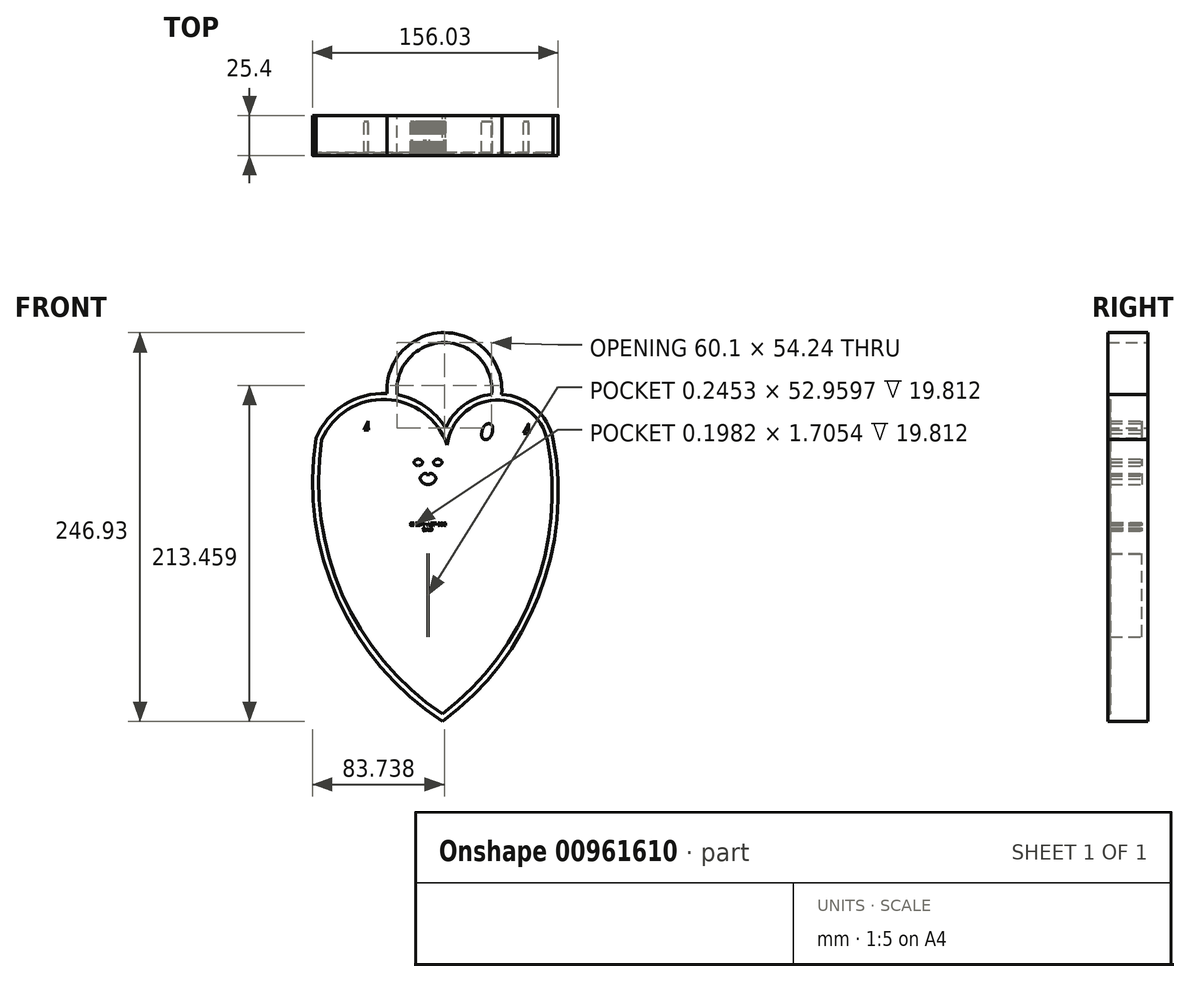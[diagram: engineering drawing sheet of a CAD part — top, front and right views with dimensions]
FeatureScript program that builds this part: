
annotation { "Feature Type Name" : "Feature", "Feature Type Description" : "" }
export const myFeature = defineFeature(function(context is Context, id is Id, definition is map)
    precondition{}
    {
        {
            var Q0;
            Q0=qCreatedBy(makeId("Front.planeOp"),FACE);
            var sketch = newSketch(context, id + "F0", { "sketchPlane" : qUnion([Q0])});
            skArc(sketch, "E0", {"start": v(8.37, 92.35) * mm, "mid": v(-4.85, 106.15) * mm, "end": v(-22.5, 113.49) * mm});
            skArc(sketch, "E1", {"start": v(76.68, 85.17) * mm, "mid": v(65.13, 104.96) * mm, "end": v(43.99, 113.8) * mm});
            skArc(sketch, "E2", {"start": v(6.5, -93.99) * mm, "mid": v(67.39, -14.51) * mm, "end": v(76.68, 85.17) * mm});
            skArc(sketch, "E3", {"start": v(-74.04, 85.97) * mm, "mid": v(-60.36, -15.9) * mm, "end": v(6.5, -93.99) * mm});
            skArc(sketch, "E4", {"start": v(37.6, 113.7) * mm, "mid": v(7.44, 146.59) * mm, "end": v(-22.5, 113.49) * mm});
            skPoint(sketch, "E4.startSnap0", {"position": v(45.14, 113.7) * mm});
            skArc(sketch, "E5.0", {"start": v(43.93, 113.12) * mm, "mid": v(7.42, 152.94) * mm, "end": v(-28.81, 112.87) * mm});
            skArc(sketch, "E6.trimOffspring", {"start": v(-28.92, 114.25) * mm, "mid": v(-55.92, 107.2) * mm, "end": v(-74.04, 85.97) * mm});
            skArc(sketch, "E7.trimOffspring", {"start": v(37.6, 113.7) * mm, "mid": v(20.11, 106.96) * mm, "end": v(8.37, 92.35) * mm});
            skSolve(sketch);
        }
        {
            var Q0;
            Q0 = qSketchRegion(id + "F0", true);
            extrude(context, id + "F1", {"entities" : qUnion([Q0]), "depth" : 25.4 * mm, "offsetDistance" : 25.4 * mm});
        }
        {
            var Q0;
            Q0 = qSketchRegion(id + "F0", true);
            extrude(context, id + "F2", {"entities" : qUnion([Q0]), "operationType" : NewBodyOperationType.ADD, "depth" : 25.4 * mm, "offsetDistance" : 25.4 * mm});
        }
        {
            var Q0;
            Q0=makeQuery(id+"F1.opExtrude","CAP_FACE",FACE,{"disambiguationData":[OSD([sQuery(id+"F0.wireOp",EDGE,"E0"),sQuery(id+"F0.wireOp",EDGE,"E1"),sQuery(id+"F0.wireOp",EDGE,"E2"),sQuery(id+"F0.wireOp",EDGE,"E3"),sQuery(id+"F0.wireOp",EDGE,"E4"),sQuery(id+"F0.wireOp",EDGE,"E5.0")])],"isStart":false});
            shell(context, id + "F3", {"entities" : qUnion([Q0]), "thickness" : 3.8 * mm});
        }
        {
            var Q0;
            Q0=makeQuery(id+"F3.opShell","OFFSET_FACE",FACE,{"disambiguationData":[OSD([sQuery(id+"F0.wireOp",EDGE,"E0"),sQuery(id+"F0.wireOp",EDGE,"E1"),sQuery(id+"F0.wireOp",EDGE,"E2"),sQuery(id+"F0.wireOp",EDGE,"E3"),sQuery(id+"F0.wireOp",EDGE,"E4"),sQuery(id+"F0.wireOp",EDGE,"E5.0")])]});
            var sketch = newSketch(context, id + "F4", { "sketchPlane" : qUnion([Q0])});
            skLineSegment(sketch, "E8", {"start": v(-21.91, 78.9) * mm, "end": v(-19.15, 68.76) * mm});
            skLineSegment(sketch, "E9", {"start": v(-19.15, 68.76) * mm, "end": v(-21.91, 65.63) * mm});
            skLineSegment(sketch, "E10", {"start": v(-21.91, 65.63) * mm, "end": v(-26.7, 65.63) * mm});
            skLineSegment(sketch, "E11", {"start": v(-26.7, 65.63) * mm, "end": v(-29.47, 68.76) * mm});
            skLineSegment(sketch, "E12", {"start": v(-29.47, 68.76) * mm, "end": v(-29.47, 73.37) * mm});
            skLineSegment(sketch, "E13", {"start": v(-29.47, 73.37) * mm, "end": v(-29.47, 76.5) * mm});
            skLineSegment(sketch, "E14", {"start": v(-29.47, 76.5) * mm, "end": v(-25.2, 78.9) * mm});
            skLineSegment(sketch, "E15", {"start": v(-25.2, 78.9) * mm, "end": v(-24.92, 78.9) * mm});
            skPoint(sketch, "E16.start.orphan", {"position": v(-2.83, 86.46) * mm});
            skLineSegment(sketch, "E17", {"start": v(-21.91, 78.9) * mm, "end": v(-22.25, 80.15) * mm});
            skLineSegment(sketch, "E18", {"start": v(-22.25, 80.15) * mm, "end": v(-16.54, 82.74) * mm});
            skPoint(sketch, "E18.endSnap0", {"position": v(-16.54, 82.51) * mm});
            skLineSegment(sketch, "E19", {"start": v(-16.54, 82.74) * mm, "end": v(-2.83, 86.46) * mm});
            skLineSegment(sketch, "E20", {"start": v(-29.47, 68.76) * mm, "end": v(-23.84, 48.1) * mm});
            skArc(sketch, "E21", {"start": v(-23.84, 48.1) * mm, "mid": v(-20.56, 42.1) * mm, "end": v(-14.93, 38.23) * mm});
            skArc(sketch, "E22", {"start": v(-16.2, 48.1) * mm, "mid": v(-9.89, 44.73) * mm, "end": v(-2.83, 45.9) * mm});
            skArc(sketch, "E23", {"start": v(-2.83, 61.75) * mm, "mid": v(-4.2, 63.46) * mm, "end": v(-6.24, 62.68) * mm});
            skArc(sketch, "E24", {"start": v(-6.24, 62.68) * mm, "mid": v(-7.41, 61.6) * mm, "end": v(-7.9, 60.1) * mm});
            skArc(sketch, "E25", {"start": v(-7.9, 60.1) * mm, "mid": v(-5.91, 57.5) * mm, "end": v(-2.83, 56.4) * mm});
            skArc(sketch, "E26", {"start": v(-6.24, 70.6) * mm, "mid": v(-8.94, 72.54) * mm, "end": v(-11.77, 70.79) * mm});
            skArc(sketch, "E27", {"start": v(-11.77, 70.79) * mm, "mid": v(-9.08, 68.4) * mm, "end": v(-6.24, 70.6) * mm});
            skLineSegment(sketch, "E28", {"start": v(-2.83, 56.4) * mm, "end": v(-2.83, 45.9) * mm});
            skArc(sketch, "E29", {"start": v(-13.44, 71.81) * mm, "mid": v(-12.75, 71.06) * mm, "end": v(-11.77, 70.79) * mm});
            skArc(sketch, "E30", {"start": v(-12.75, 72.46) * mm, "mid": v(-11.98, 71.93) * mm, "end": v(-11.06, 71.77) * mm});
            skPoint(sketch, "E30.startSnap0", {"position": v(-12.75, 71.06) * mm});
            skArc(sketch, "E31", {"start": v(-20.39, 37.98) * mm, "mid": v(-17.62, 37.33) * mm, "end": v(-14.93, 38.23) * mm});
            skArc(sketch, "E32", {"start": v(-20.39, 37.98) * mm, "mid": v(-21.76, 24.2) * mm, "end": v(-23.02, 10.41) * mm});
            skArc(sketch, "E33", {"start": v(-23.02, 10.41) * mm, "mid": v(-22.18, -1.83) * mm, "end": v(-20.39, -13.98) * mm});
            skArc(sketch, "E34", {"start": v(-20.39, -13.98) * mm, "mid": v(-22.78, -15.3) * mm, "end": v(-25.05, -16.81) * mm});
            skArc(sketch, "E35", {"start": v(-25.05, -16.81) * mm, "mid": v(-26.57, -24.06) * mm, "end": v(-25.05, -31.3) * mm});
            skArc(sketch, "E36", {"start": v(-29.32, -35.4) * mm, "mid": v(-25.75, -34.85) * mm, "end": v(-25.05, -31.3) * mm});
            skArc(sketch, "E37", {"start": v(-29.32, -35.4) * mm, "mid": v(-31.45, -37.49) * mm, "end": v(-30.2, -40.2) * mm});
            skArc(sketch, "E38", {"start": v(-30.2, -40.2) * mm, "mid": v(-25.41, -41.87) * mm, "end": v(-20.62, -40.2) * mm});
            skArc(sketch, "E39", {"start": v(-9, -40.2) * mm, "mid": v(-14.81, -38.24) * mm, "end": v(-20.62, -40.2) * mm});
            skArc(sketch, "E40", {"start": v(-9, -42.9) * mm, "mid": v(-8.38, -41.55) * mm, "end": v(-9, -40.2) * mm});
            skArc(sketch, "E41", {"start": v(-9, -42.9) * mm, "mid": v(-6.43, -45.73) * mm, "end": v(-2.83, -44.43) * mm});
            skArc(sketch, "E42", {"start": v(-2.83, -44.43) * mm, "mid": v(-2.7, -42.4) * mm, "end": v(-2.83, -40.38) * mm});
            skLineSegment(sketch, "E43", {"start": v(-2.83, -40.38) * mm, "end": v(-2.7, 12.58) * mm});
            skPoint(sketch, "E43.endSnap0", {"position": v(-2.7, -42.4) * mm});
            skLineSegment(sketch, "E44", {"start": v(-2.7, 12.23) * mm, "end": v(-2.95, 12.58) * mm});
            skPoint(sketch, "E45.end.orphan", {"position": v(-7.53, 10.41) * mm});
            skArc(sketch, "E46", {"start": v(-5.32, 80.19) * mm, "mid": v(-5.15, 83.03) * mm, "end": v(-6.72, 85.4) * mm});
            skArc(sketch, "E47", {"start": v(-8.27, 77.24) * mm, "mid": v(-6.15, 78.07) * mm, "end": v(-5.32, 80.19) * mm});
            skArc(sketch, "E48", {"start": v(-8.27, 77.24) * mm, "mid": v(-5.55, 75.7) * mm, "end": v(-2.83, 77.24) * mm});
            skArc(sketch, "E49.MirrorCS", {"start": v(7.1, 72.46) * mm, "mid": v(6.32, 71.93) * mm, "end": v(5.4, 71.77) * mm});
            skArc(sketch, "E50.MirrorCS", {"start": v(7.78, 71.81) * mm, "mid": v(7.1, 71.06) * mm, "end": v(6.11, 70.79) * mm});
            skLineSegment(sketch, "E51.MirrorCS", {"start": v(19.55, 78.9) * mm, "end": v(19.26, 78.9) * mm});
            skLineSegment(sketch, "E52.MirrorCS", {"start": v(23.8, 76.5) * mm, "end": v(19.55, 78.9) * mm});
            skArc(sketch, "E53.MirrorCS", {"start": v(3.35, -42.9) * mm, "mid": v(2.72, -41.55) * mm, "end": v(3.35, -40.2) * mm});
            skLineSegment(sketch, "E54.MirrorCS", {"start": v(21.04, 65.63) * mm, "end": v(23.8, 68.76) * mm});
            skArc(sketch, "E55.MirrorCS", {"start": v(-2.83, -44.43) * mm, "mid": v(-2.96, -42.4) * mm, "end": v(-2.83, -40.38) * mm});
            skArc(sketch, "E56.MirrorCS", {"start": v(-2.83, 61.75) * mm, "mid": v(-1.46, 63.46) * mm, "end": v(0.58, 62.68) * mm});
            skLineSegment(sketch, "E57.MirrorCS", {"start": v(23.8, 73.37) * mm, "end": v(23.8, 76.5) * mm});
            skLineSegment(sketch, "E58.MirrorCS", {"start": v(23.8, 68.76) * mm, "end": v(23.8, 73.37) * mm});
            skLineSegment(sketch, "E59.MirrorCS", {"start": v(16.25, 65.63) * mm, "end": v(21.04, 65.63) * mm});
            skLineSegment(sketch, "E60.MirrorCS", {"start": v(13.49, 68.76) * mm, "end": v(16.25, 65.63) * mm});
            skArc(sketch, "E61.MirrorCS", {"start": v(0.58, 62.68) * mm, "mid": v(1.75, 61.6) * mm, "end": v(2.24, 60.1) * mm});
            skLineSegment(sketch, "E62.MirrorCS", {"start": v(16.25, 78.9) * mm, "end": v(16.6, 80.15) * mm});
            skArc(sketch, "E63.MirrorCS", {"start": v(23.66, -35.4) * mm, "mid": v(20.1, -34.85) * mm, "end": v(19.38, -31.3) * mm});
            skLineSegment(sketch, "E64.MirrorCS", {"start": v(16.6, 80.15) * mm, "end": v(10.88, 82.74) * mm});
            skArc(sketch, "E65.MirrorCS", {"start": v(0.58, 70.6) * mm, "mid": v(3.28, 72.54) * mm, "end": v(6.11, 70.79) * mm});
            skArc(sketch, "E66.MirrorCS", {"start": v(6.11, 70.79) * mm, "mid": v(3.42, 68.4) * mm, "end": v(0.58, 70.6) * mm});
            skArc(sketch, "E67.MirrorCS", {"start": v(2.6, 77.24) * mm, "mid": v(0.49, 78.07) * mm, "end": v(-0.34, 80.19) * mm});
            skArc(sketch, "E68.MirrorCS", {"start": v(10.54, 48.1) * mm, "mid": v(4.23, 44.73) * mm, "end": v(-2.83, 45.9) * mm});
            skPoint(sketch, "E69.MirrorP", {"position": v(7.1, 71.06) * mm});
            skLineSegment(sketch, "E70.MirrorCS", {"start": v(-2.83, -40.38) * mm, "end": v(-2.95, 12.58) * mm});
            skArc(sketch, "E71.MirrorCS", {"start": v(2.24, 60.1) * mm, "mid": v(0.25, 57.5) * mm, "end": v(-2.83, 56.4) * mm});
            skArc(sketch, "E72.MirrorCS", {"start": v(14.73, -13.98) * mm, "mid": v(17.11, -15.3) * mm, "end": v(19.38, -16.81) * mm});
            skArc(sketch, "E73.MirrorCS", {"start": v(-0.34, 80.19) * mm, "mid": v(-0.5, 83.03) * mm, "end": v(1.06, 85.4) * mm});
            skArc(sketch, "E74.MirrorCS", {"start": v(24.55, -40.2) * mm, "mid": v(19.75, -41.87) * mm, "end": v(14.96, -40.2) * mm});
            skLineSegment(sketch, "E75.MirrorCS", {"start": v(-2.95, 12.23) * mm, "end": v(-2.7, 12.58) * mm});
            skArc(sketch, "E76.MirrorCS", {"start": v(3.35, -42.9) * mm, "mid": v(0.77, -45.73) * mm, "end": v(-2.83, -44.43) * mm});
            skPoint(sketch, "E77.MirrorP", {"position": v(-2.96, -42.4) * mm});
            skArc(sketch, "E78.MirrorCS", {"start": v(2.6, 77.24) * mm, "mid": v(-0.11, 75.7) * mm, "end": v(-2.83, 77.24) * mm});
            skArc(sketch, "E79.MirrorCS", {"start": v(18.18, 48.1) * mm, "mid": v(14.9, 42.1) * mm, "end": v(9.27, 38.23) * mm});
            skPoint(sketch, "E80.MirrorP", {"position": v(10.88, 82.51) * mm});
            skPoint(sketch, "E81.MirrorP", {"position": v(1.87, 10.41) * mm});
            skArc(sketch, "E82.MirrorCS", {"start": v(19.38, -16.81) * mm, "mid": v(20.9, -24.06) * mm, "end": v(19.38, -31.3) * mm});
            skArc(sketch, "E83.MirrorCS", {"start": v(23.66, -35.4) * mm, "mid": v(25.79, -37.49) * mm, "end": v(24.55, -40.2) * mm});
            skArc(sketch, "E84.MirrorCS", {"start": v(3.35, -40.2) * mm, "mid": v(9.15, -38.24) * mm, "end": v(14.96, -40.2) * mm});
            skArc(sketch, "E85.MirrorCS", {"start": v(17.36, 10.41) * mm, "mid": v(16.51, -1.83) * mm, "end": v(14.73, -13.98) * mm});
            skArc(sketch, "E86.MirrorCS", {"start": v(14.73, 37.98) * mm, "mid": v(11.96, 37.33) * mm, "end": v(9.27, 38.23) * mm});
            skArc(sketch, "E87.MirrorCS", {"start": v(14.73, 37.98) * mm, "mid": v(16.1, 24.2) * mm, "end": v(17.36, 10.41) * mm});
            skLineSegment(sketch, "E88.MirrorCS", {"start": v(16.25, 78.9) * mm, "end": v(13.49, 68.76) * mm});
            skLineSegment(sketch, "E89.MirrorCS", {"start": v(23.8, 68.76) * mm, "end": v(18.18, 48.1) * mm});
            skArc(sketch, "E90.MirrorCS", {"start": v(-2.83, 86.46) * mm, "mid": v(10.88, 82.51) * mm, "end": v(23.8, 76.5) * mm});
            skPoint(sketch, "E91.orphan", {"position": v(-2.96, 16.22) * mm});
            skPoint(sketch, "E92.end.orphan", {"position": v(1.3, 6.37) * mm});
            skPoint(sketch, "E93.orphan", {"position": v(-6.97, 6.37) * mm});
            skPoint(sketch, "E94.orphan", {"position": v(-2.7, 16.22) * mm});
            skText(sketch, "E95", { "text": "SEIZURE ALERT DOG\n             S.A.D", "fontName": "OpenSans-Regular.ttf"});
            skPoint(sketch, "E96.orphan", {"position": v(-2.83, 38.9) * mm});
            skPoint(sketch, "E97.MirrorCS.end.orphan", {"position": v(4.45, 4.42) * mm});
            skPoint(sketch, "E98.end.orphan", {"position": v(-10.11, 4.42) * mm});
            skPoint(sketch, "E99.MirrorCS.end.orphan", {"position": v(2.93, -32.6) * mm});
            skPoint(sketch, "E100.end.orphan", {"position": v(-8.6, -32.6) * mm});
            skLineSegment(sketch, "E101", {"start": v(-25.2, 78.9) * mm, "end": v(-22.25, 80.15) * mm});
            skLineSegment(sketch, "E102", {"start": v(-20.39, 37.98) * mm, "end": v(-2.7, 12.23) * mm});
            skLineSegment(sketch, "E103", {"start": v(-2.7, 12.58) * mm, "end": v(14.73, 37.98) * mm});
            skArc(sketch, "E104", {"start": v(-14.93, 38.23) * mm, "mid": v(-8.73, 35.8) * mm, "end": v(-2.83, 38.9) * mm});
            skArc(sketch, "E105", {"start": v(-2.83, 38.9) * mm, "mid": v(3.07, 35.85) * mm, "end": v(9.27, 38.23) * mm});
            skLineSegment(sketch, "E106", {"start": v(-9, -40.2) * mm, "end": v(-11.4, 2.24) * mm});
            skLineSegment(sketch, "E107", {"start": v(3.35, -40.2) * mm, "end": v(6.25, 2.45) * mm});
            skText(sketch, "E108", { "text": "JAM", "fontName": "OpenSans-BoldItalic.ttf"});
            skText(sketch, "E109", { "text": "LOLA", "fontName": "OpenSans-BoldItalic.ttf"});
            const initialGuessF4  = {"E95": [-0.01407, 0.03038, 1, 0, 0.00172], "E108": [-0.05383, 0.08579, 1, 0, 0.01292], "E109": [0.01594, 0.08256, 1, 0, 0.01507]};
            skSetInitialGuess(sketch, initialGuessF4);
            skSolve(sketch);
        }
        {
            var Q0;
            Q0=makeQuery(id+"F4.imprint","IMPRINT",FACE,{"disambiguationData":[TD([[makeQuery(id+"F4.imprint","IMPRINT",EDGE,{"derivedFrom":sQuery(id+"F4.wireOp",EDGE,"E108.sketch_text.stroke-0")}),-1.0]])]});
            var Q1;
            Q1=makeQuery(id+"F4.imprint","IMPRINT",FACE,{"disambiguationData":[TD([[makeQuery(id+"F4.imprint","IMPRINT",EDGE,{"derivedFrom":sQuery(id+"F4.wireOp",EDGE,"E108.sketch_text.stroke-24")}),-1.0]])]});
            var Q2;
            Q2=makeQuery(id+"F4.imprint","IMPRINT",FACE,{"disambiguationData":[TD([[makeQuery(id+"F4.imprint","IMPRINT",EDGE,{"derivedFrom":sQuery(id+"F4.wireOp",EDGE,"E109.sketch_text.stroke-0")}),-1.0]])]});
            var Q3;
            Q3=makeQuery(id+"F4.imprint","IMPRINT",FACE,{"disambiguationData":[TD([[makeQuery(id+"F4.imprint","IMPRINT",EDGE,{"derivedFrom":sQuery(id+"F4.wireOp",EDGE,"E109.sketch_text.stroke-26")}),-1.0]])]});
            var Q4;
            Q4=makeQuery(id+"F4.imprint","IMPRINT",FACE,{"disambiguationData":[TD([[makeQuery(id+"F4.imprint","IMPRINT",EDGE,{"derivedFrom":sQuery(id+"F4.wireOp",EDGE,"E8")}),-1.0]])]});
            var Q5;
            Q5=makeQuery(id+"F4.imprint","IMPRINT",FACE,{"disambiguationData":[TD([[makeQuery(id+"F4.imprint","IMPRINT",EDGE,{"derivedFrom":sQuery(id+"F4.wireOp",EDGE,"E42")}),1.0]])]});
            var Q6;
            {var subQ0=sQuery(id+"F4.wireOp",EDGE,"E51.MirrorCS");Q6=makeQuery(id+"F4.imprint","IMPRINT",FACE,{"disambiguationData":[TD([[makeQuery(id+"F4.imprint","IMPRINT",EDGE,{"derivedFrom":subQ0}),1.0]])]});}
            var Q7;
            Q7=makeQuery(id+"F4.imprint","IMPRINT",FACE,{"disambiguationData":[TD([[makeQuery(id+"F4.imprint","IMPRINT",EDGE,{"derivedFrom":sQuery(id+"F4.wireOp",EDGE,"E108.sketch_text.stroke-10")}),-1.0]])]});
            var Q8;
            Q8=makeQuery(id+"F4.imprint","IMPRINT",FACE,{"disambiguationData":[TD([[makeQuery(id+"F4.imprint","IMPRINT",EDGE,{"derivedFrom":sQuery(id+"F4.wireOp",EDGE,"E109.sketch_text.stroke-6")}),-1.0]])]});
            var Q9;
            Q9=makeQuery(id+"F4.imprint","IMPRINT",FACE,{"disambiguationData":[TD([[makeQuery(id+"F4.imprint","IMPRINT",EDGE,{"derivedFrom":sQuery(id+"F4.wireOp",EDGE,"E109.sketch_text.stroke-32")}),-1.0]])]});
            var Q10;
            {var subQ5=sQuery(id+"F4.wireOp",EDGE,"E32");Q10=makeQuery(id+"F4.imprint","IMPRINT",FACE,{"disambiguationData":[TD([[makeQuery(id+"F4.imprint","IMPRINT",EDGE,{"derivedFrom":subQ5}),1.0]])]});}
            var Q11;
            {var subQ0=sQuery(id+"F4.wireOp",EDGE,"E42");Q11=makeQuery(id+"F4.imprint","IMPRINT",FACE,{"disambiguationData":[TD([[makeQuery(id+"F4.imprint","IMPRINT",EDGE,{"derivedFrom":subQ0}),-1.0]])]});}
            var Q12;
            {var subQ0=sQuery(id+"F4.wireOp",EDGE,"E31");Q12=makeQuery(id+"F4.imprint","IMPRINT",FACE,{"disambiguationData":[TD([[makeQuery(id+"F4.imprint","IMPRINT",EDGE,{"derivedFrom":subQ0}),-1.0]])]});}
            var Q13;
            {var subQ0=sQuery(id+"F4.wireOp",EDGE,"E90.MirrorCS");var subQ1=sQuery(id+"F0.wireOp",EDGE,"E0");var subQ3=sQuery(id+"F0.wireOp",EDGE,"E1");var subQ4=makeQuery(id+"F0.imprint","INTERSECT",VERTEX,{"derivedFrom":[subQ1,subQ3]});var subQ6=makeQuery(id+"F3.opShell","OFFSET_EDGE",EDGE,{"disambiguationData":[OSD([subQ1]),TDD([makeQuery(id+"F1.opExtrude","CAP_EDGE",EDGE,{"disambiguationData":[OSD([subQ1]),TDD([makeQuery(id+"F0.imprint","IMPRINT",EDGE,{"disambiguationData":[TD([[subQ4,-1.0]])],"derivedFrom":subQ1})])],"isStart":true}),makeQuery(id+"F1.opExtrude","CAP_EDGE",EDGE,{"disambiguationData":[OSD([subQ1]),TDD([makeQuery(id+"F0.imprint","IMPRINT",EDGE,{"disambiguationData":[TD([[makeQuery(id+"F0.imprint","INTERSECT",VERTEX,{"derivedFrom":[subQ1,sQuery(id+"F0.wireOp",EDGE,"E3")]}),1.0]])],"derivedFrom":subQ1})])],"isStart":true})])]});var subQ7=makeQuery(id+"F4.imprint","INTERSECT",VERTEX,{"derivedFrom":[subQ6,subQ0]});Q13=makeQuery(id+"F4.imprint","IMPRINT",FACE,{"disambiguationData":[TD([[makeQuery(id+"F4.imprint","IMPRINT",EDGE,{"disambiguationData":[TD([[subQ7,-1.0]])],"derivedFrom":subQ0}),-1.0]])]});}
            var Q14;
            Q14=makeQuery(id+"F4.imprint","IMPRINT",FACE,{"disambiguationData":[TD([[makeQuery(id+"F4.imprint","IMPRINT",EDGE,{"derivedFrom":sQuery(id+"F4.wireOp",EDGE,"E8")}),1.0]])]});
            var Q15;
            Q15=makeQuery(id+"F4.imprint","IMPRINT",FACE,{"disambiguationData":[TD([[makeQuery(id+"F4.imprint","IMPRINT",EDGE,{"derivedFrom":sQuery(id+"F4.wireOp",EDGE,"E54.MirrorCS")}),1.0]])]});
            extrude(context, id + "F5", {"entities" : qUnion([Q0, Q1, Q2, Q3, Q4, Q5, Q6, Q7, Q8, Q9, Q10, Q11, Q12, Q13, Q14, Q15]), "operationType" : NewBodyOperationType.ADD, "depth" : 19.8 * mm, "offsetDistance" : 25.4 * mm});
        }
    });
